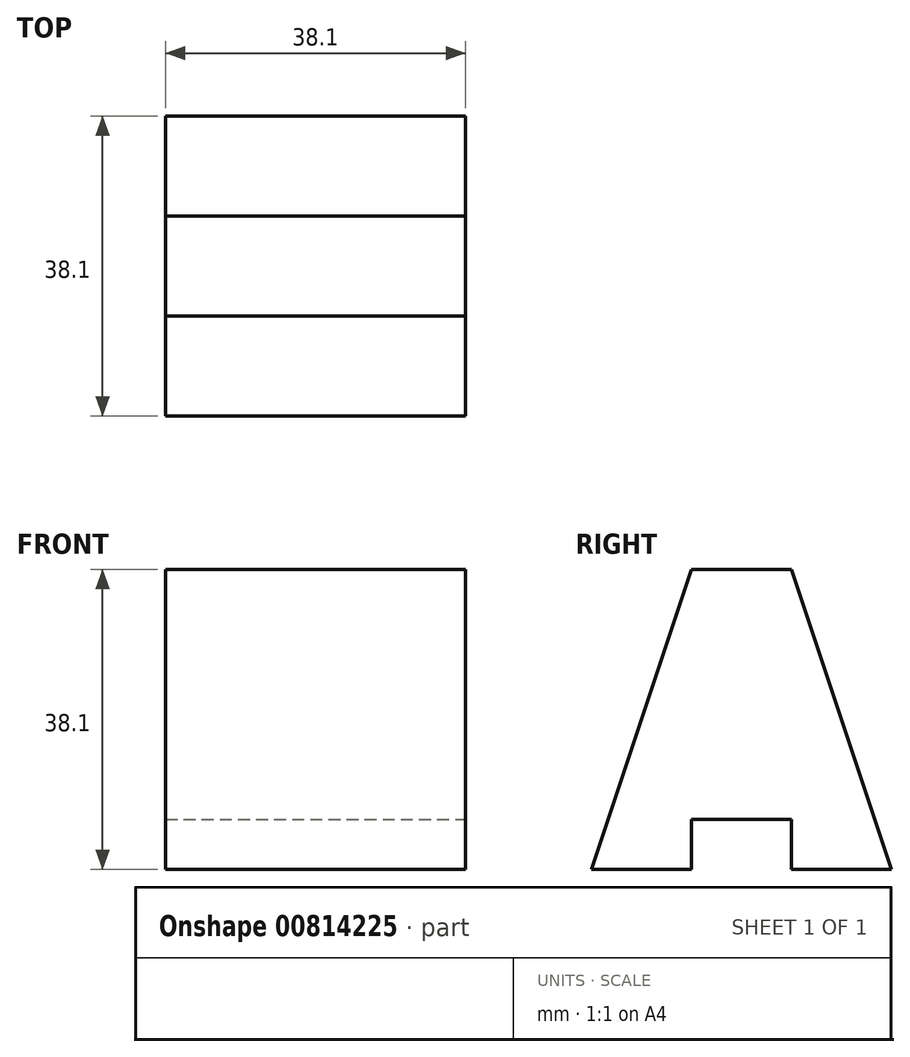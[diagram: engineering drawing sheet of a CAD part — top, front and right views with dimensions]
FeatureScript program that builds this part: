
annotation { "Feature Type Name" : "Feature", "Feature Type Description" : "" }
export const myFeature = defineFeature(function(context is Context, id is Id, definition is map)
    precondition{}
    {
        {
            var Q0;
            Q0=qCreatedBy(makeId("Top.planeOp"),FACE);
            var sketch = newSketch(context, id + "F0", { "sketchPlane" : qUnion([Q0])});
            skLineSegment(sketch, "E0", {"start": v(0, 0) * mm, "end": v(0, 38.1) * mm});
            skLineSegment(sketch, "E1", {"start": v(0, 38.1) * mm, "end": v(38.1, 38.1) * mm});
            skLineSegment(sketch, "E2", {"start": v(38.1, 38.1) * mm, "end": v(38.1, 0) * mm});
            skLineSegment(sketch, "E3", {"start": v(0, 0) * mm, "end": v(38.1, 0) * mm});
            skSolve(sketch);
        }
        {
            var Q0;
            Q0 = qSketchRegion(id + "F0", true);
            extrude(context, id + "F1", {"entities" : qUnion([Q0]), "depth" : 38.1 * mm, "offsetDistance" : 25.4 * mm});
        }
        {
            var Q0;
            Q0=makeQuery(id+"F1.opExtrude","SWEPT_FACE",FACE,{"disambiguationData":[OSD([sQuery(id+"F0.wireOp",EDGE,"E2")])]});
            var sketch = newSketch(context, id + "F2", { "sketchPlane" : qUnion([Q0])});
            skLineSegment(sketch, "E4", {"start": v(0, 0) * mm, "end": v(12.7, 0) * mm});
            skLineSegment(sketch, "E5", {"start": v(12.7, 0) * mm, "end": v(12.7, 6.35) * mm});
            skLineSegment(sketch, "E6", {"start": v(12.7, 6.35) * mm, "end": v(25.4, 6.35) * mm});
            skLineSegment(sketch, "E7", {"start": v(25.4, 6.35) * mm, "end": v(25.4, 0) * mm});
            skLineSegment(sketch, "E8", {"start": v(25.4, 0) * mm, "end": v(38.1, 0) * mm});
            skLineSegment(sketch, "E9", {"start": v(25.4, 38.1) * mm, "end": v(38.1, 0) * mm});
            skLineSegment(sketch, "E10", {"start": v(12.68, 38.1) * mm, "end": v(0, 0) * mm});
            skLineSegment(sketch, "E11", {"start": v(0, 38.1) * mm, "end": v(12.68, 38.1) * mm});
            skLineSegment(sketch, "E12", {"start": v(0, 38.1) * mm, "end": v(0, 0) * mm});
            skLineSegment(sketch, "E13", {"start": v(25.4, 38.1) * mm, "end": v(38.1, 38.1) * mm});
            skLineSegment(sketch, "E14", {"start": v(38.1, 38.1) * mm, "end": v(38.1, 0) * mm});
            skLineSegment(sketch, "E15", {"start": v(12.7, 0) * mm, "end": v(25.4, 0) * mm});
            skSolve(sketch);
        }
        {
            var Q0;
            Q0=makeQuery(id+"F2.imprint","IMPRINT",FACE,{"disambiguationData":[TD([[makeQuery(id+"F2.imprint","IMPRINT",EDGE,{"derivedFrom":sQuery(id+"F2.wireOp",EDGE,"E10")}),-1.0]])]});
            extrude(context, id + "F3", {"entities" : qUnion([Q0]), "operationType" : NewBodyOperationType.REMOVE, "oppositeDirection" : true, "depth" : 38.1 * mm, "offsetDistance" : 25.4 * mm});
        }
        {
            var Q0;
            Q0 = qSketchRegion(id + "F2", true);
            extrude(context, id + "F4", {"entities" : qUnion([Q0]), "operationType" : NewBodyOperationType.REMOVE, "oppositeDirection" : true, "depth" : 38.1 * mm, "offsetDistance" : 25.4 * mm});
        }
    });
